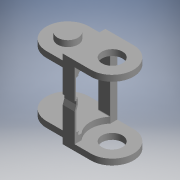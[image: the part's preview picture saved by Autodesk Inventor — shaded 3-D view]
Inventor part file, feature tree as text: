
AUTODESK INVENTOR PART (.ipt)
format: ipt  version: 2017.3 (Build 213256000, 256)  size: 223,744 bytes
history: native  units: mm (DEFAULTED — no unit token found)
features: other x35, extrude x11, sketch x11
ambient origin geometry x8: Origin, YZ Plane, XZ Plane, XY Plane, X Axis, Y Axis, Z Axis, Center Point
bodies: Solid1 (feature_tree)
feature tree (57):
  extrude  "Extrusion1"  Depth=1.75mm TaperAngle=0.0deg
  sketch  "Sketch_3"  dims[d4=1.75mm d5=0.0mm d6=3.5mm d7=0.0mm]
  sketch  "Sketch_6"  dims[d16=3.5mm d17=0.0mm d18=9.75mm d19=0.0mm]
  sketch  "Sketch_7"  dims[d20=9.75mm d21=0.0mm d22=0.0mm d23=0.0mm d24=0.0mm d25=0.0mm]
  sketch  "Sketch_4"  dims[d8=3.5mm d9=0.0mm d10=1.75mm d11=0.0mm]
  extrude  "Extrusion2"  Depth=3.5mm TaperAngle=0.0deg
  extrude  "Extrusion3"  Depth=1.75mm TaperAngle=0.0deg
  extrude  "Extrusion4"  Depth=1.75mm TaperAngle=0.0deg
  extrude  "Extrusion5"  Depth=9.75mm TaperAngle=0.0deg
  sketch  "Sketch_12"
  extrude  "Extrusion6"  TaperAngle=0.0deg  [1 undecoded]
  extrude  "Extrusion7"  [1 undecoded]
  extrude  "Extrusion8"  [1 undecoded]
  extrude  "Extrusion9"  [1 undecoded]
  extrude  "Extrusion10"  [1 undecoded]
  extrude  "Extrusion11"  [1 undecoded]
  other  "R1_XY"
  other  "R1_YZ"
  other  "R1_ZX"
  other  "R1_X"
  other  "R1_Y"
  other  "R1_Z"
  other  "R1_Center"
  other  "clip_to_dummy_XY"
  other  "clip_to_dummy_YZ"
  other  "clip_to_dummy_ZX"
  other  "clip_to_dummy_X"
  other  "clip_to_dummy_Y"
  other  "clip_to_dummy_Z"
  other  "clip_to_dummy_Center"
  other  "move_1_XY"
  other  "move_1_YZ"
  other  "move_1_ZX"
  other  "move_1_X"
  other  "move_1_Y"
  other  "move_1_Z"
  other  "move_1_Center"
  other  "move_2_XY"
  other  "move_2_YZ"
  other  "move_2_ZX"
  other  "move_2_X"
  other  "move_2_Y"
  other  "move_2_Z"
  other  "move_2_Center"
  other  "move_end_XY"
  other  "move_end_YZ"
  other  "move_end_ZX"
  other  "move_end_X"
  other  "move_end_Y"
  other  "move_end_Z"
  other  "move_end_Center"
  sketch  "Sketch_1"  dims[d0=1.75mm d1=0.0mm d2=1.75mm d3=0.0mm]
  sketch  "Sketch_5"  dims[d12=1.75mm d13=0.0mm d14=1.75mm d15=0.0mm]
  sketch  "Sketch_9"
  sketch  "Sketch_11"
  sketch  "Sketch_19"
  sketch  "Sketch_20"
note: 6 required parameter values undecoded (feature->parameter linkage not recoverable at this tier; creation-order binding heuristic only, values carry confidence <= 0.55)
